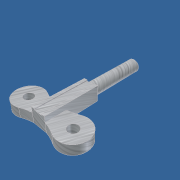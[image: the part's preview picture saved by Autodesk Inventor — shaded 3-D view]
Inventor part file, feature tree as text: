
AUTODESK INVENTOR PART (.ipt)
format: ipt  version: unknown  size: 211,456 bytes
history: native  units: mm
features: extrude x3, sketch x3
ambient origin geometry x8: Origin, YZ Plane, XZ Plane, XY Plane, X Axis, Y Axis, Z Axis, Center Point
feature tree (6):
  extrude  "Выдавливание1"  Depth=15.75mm
  extrude  "Выдавливание4"  Depth=3.0mm
  extrude  "Выдавливание5"  Depth=3.0mm
  sketch  "Эскиз1"
  sketch  "Эскиз4"
  sketch  "Эскиз5"
